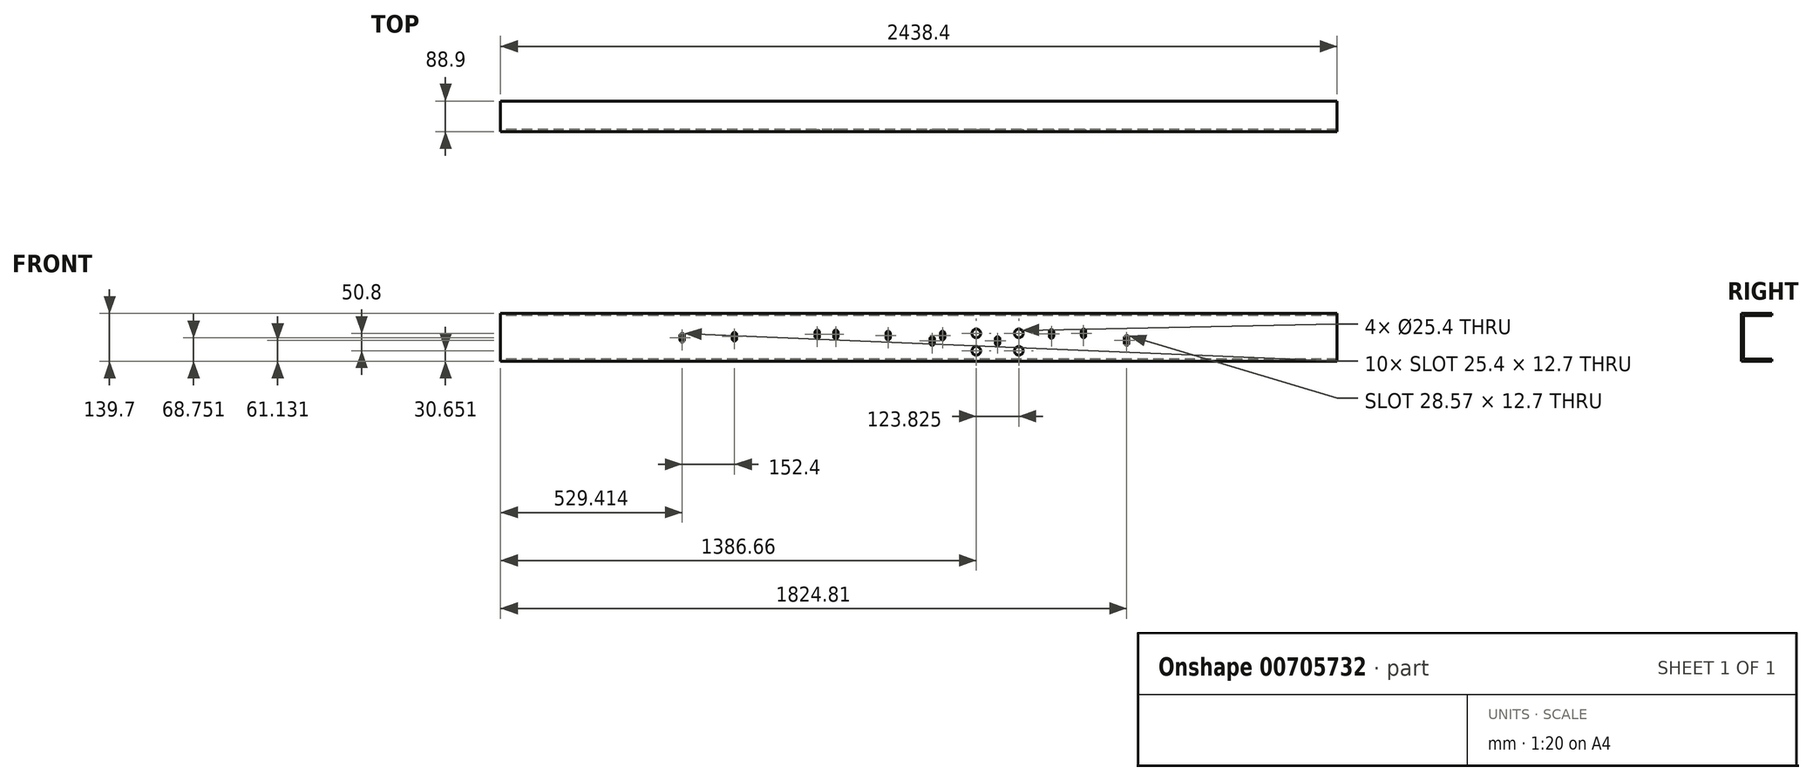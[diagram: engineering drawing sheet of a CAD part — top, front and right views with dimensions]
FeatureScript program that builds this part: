
annotation { "Feature Type Name" : "Feature", "Feature Type Description" : "" }
export const myFeature = defineFeature(function(context is Context, id is Id, definition is map)
    precondition{}
    {
        {
            var Q0;
            Q0=qCreatedBy(makeId("Right.planeOp"),FACE);
            var sketch = newSketch(context, id + "F0", { "sketchPlane" : qUnion([Q0])});
            skLineSegment(sketch, "E0.bottom", {"start": v(44.45, 69.85) * mm, "end": v(-44.45, 69.85) * mm});
            skLineSegment(sketch, "E0.top", {"start": v(44.45, -69.85) * mm, "end": v(-44.45, -69.85) * mm});
            skLineSegment(sketch, "E0.left", {"start": v(44.45, 69.85) * mm, "end": v(44.45, -69.85) * mm});
            skLineSegment(sketch, "E0.right", {"start": v(-44.45, 69.85) * mm, "end": v(-44.45, -69.85) * mm});
            skPoint(sketch, "E0.middle", {"position": v(0, 0) * mm});
            skSolve(sketch);
        }
        {
            var Q0;
            Q0 = qSketchRegion(id + "F0", true);
            extrude(context, id + "F1", {"entities" : qUnion([Q0]), "depth" : 2438.4 * mm, "offsetDistance" : 25.4 * mm, "symmetric" : true});
        }
        {
            var Q0;
            Q0=makeQuery(id+"F1.opExtrude","CAP_FACE",FACE,{"disambiguationData":[OSD([sQuery(id+"F0.wireOp",EDGE,"E0.bottom"),sQuery(id+"F0.wireOp",EDGE,"E0.top"),sQuery(id+"F0.wireOp",EDGE,"E0.left"),sQuery(id+"F0.wireOp",EDGE,"E0.right")])],"isStart":true});
            var sketch = newSketch(context, id + "F2", { "sketchPlane" : qUnion([Q0])});
            skLineSegment(sketch, "E1", {"start": v(-44.45, 63.5) * mm, "end": v(38.1, 63.5) * mm});
            skLineSegment(sketch, "E2", {"start": v(38.1, 63.5) * mm, "end": v(38.1, -63.5) * mm});
            skLineSegment(sketch, "E3", {"start": v(38.1, -63.5) * mm, "end": v(-44.45, -63.5) * mm});
            skSolve(sketch);
        }
        {
            var Q0;
            {var subQ0=sQuery(id+"F2.wireOp",EDGE,"E1");Q0=makeQuery(id+"F2.imprint","IMPRINT",FACE,{"disambiguationData":[TD([[makeQuery(id+"F2.imprint","IMPRINT",EDGE,{"derivedFrom":subQ0}),-1.0]])]});}
            extrude(context, id + "F3", {"entities" : qUnion([Q0]), "operationType" : NewBodyOperationType.REMOVE, "endBound" : BoundingType.THROUGH_ALL, "oppositeDirection" : true, "depth" : 25.4 * mm, "offsetDistance" : 25.4 * mm});
        }
        {
            var Q0;
            Q0=makeQuery(id+"F1.opExtrude","SWEPT_FACE",FACE,{"disambiguationData":[OSD([sQuery(id+"F0.wireOp",EDGE,"E0.right")])]});
            var sketch = newSketch(context, id + "F4", { "sketchPlane" : qUnion([Q0])});
            skLineSegment(sketch, "E4.bottom", {"start": v(-689.79, 11.6) * mm, "end": v(-689.79, 11.6) * mm});
            skLineSegment(sketch, "E4.top", {"start": v(-689.79, -13.8) * mm, "end": v(-689.79, -13.8) * mm});
            skLineSegment(sketch, "E4.left", {"start": v(-696.14, 5.25) * mm, "end": v(-696.14, -7.45) * mm});
            skLineSegment(sketch, "E4.right", {"start": v(-683.44, 5.25) * mm, "end": v(-683.44, -7.45) * mm});
            skPoint(sketch, "E4.middle", {"position": v(-689.79, -1.1) * mm});
            skPoint(sketch, "E4.middle.positionSnap0", {"position": v(-689.79, -14.24) * mm});
            skPoint(sketch, "E4.middle.positionSnap1", {"position": v(-696.33, -1.1) * mm});
            skPoint(sketch, "E4.centerSnap0", {"position": v(-689.79, -14.24) * mm});
            skPoint(sketch, "E4.centerSnap1", {"position": v(-696.33, -1.1) * mm});
            skLineSegment(sketch, "E5.bottom", {"start": v(-537.39, 14.78) * mm, "end": v(-537.39, 14.78) * mm});
            skLineSegment(sketch, "E5.top", {"start": v(-537.39, -10.62) * mm, "end": v(-537.39, -10.62) * mm});
            skLineSegment(sketch, "E5.left", {"start": v(-543.74, 8.43) * mm, "end": v(-543.74, -4.27) * mm});
            skLineSegment(sketch, "E5.right", {"start": v(-531.04, 8.43) * mm, "end": v(-531.04, -4.27) * mm});
            skPoint(sketch, "E5.middle", {"position": v(-537.39, 2.08) * mm});
            skPoint(sketch, "E5.middle.positionSnap0", {"position": v(-537.39, -11.13) * mm});
            skPoint(sketch, "E5.middle.positionSnap1", {"position": v(-543.99, 2.08) * mm});
            skPoint(sketch, "E5.centerSnap0", {"position": v(-537.39, -11.13) * mm});
            skPoint(sketch, "E5.centerSnap1", {"position": v(-543.99, 2.08) * mm});
            skLineSegment(sketch, "E6.bottom", {"start": v(-296.09, 21.38) * mm, "end": v(-296.09, 21.38) * mm});
            skLineSegment(sketch, "E6.top", {"start": v(-296.09, -4.02) * mm, "end": v(-296.09, -4.02) * mm});
            skLineSegment(sketch, "E6.left", {"start": v(-302.44, 15.03) * mm, "end": v(-302.44, 2.33) * mm});
            skLineSegment(sketch, "E6.right", {"start": v(-289.74, 15.03) * mm, "end": v(-289.74, 2.33) * mm});
            skPoint(sketch, "E6.middle", {"position": v(-296.09, 8.68) * mm});
            skPoint(sketch, "E6.middle.positionSnap0", {"position": v(-296.09, -4.53) * mm});
            skPoint(sketch, "E6.middle.positionSnap1", {"position": v(-302.69, 8.68) * mm});
            skPoint(sketch, "E6.centerSnap0", {"position": v(-296.09, -4.53) * mm});
            skPoint(sketch, "E6.centerSnap1", {"position": v(-302.69, 8.68) * mm});
            skLineSegment(sketch, "E7.bottom", {"start": v(-242.11, 21.38) * mm, "end": v(-242.11, 21.38) * mm});
            skLineSegment(sketch, "E7.top", {"start": v(-242.11, -4.02) * mm, "end": v(-242.11, -4.02) * mm});
            skLineSegment(sketch, "E7.left", {"start": v(-248.46, 15.03) * mm, "end": v(-248.46, 2.33) * mm});
            skLineSegment(sketch, "E7.right", {"start": v(-235.76, 15.03) * mm, "end": v(-235.76, 2.33) * mm});
            skPoint(sketch, "E7.middle", {"position": v(-242.11, 8.68) * mm});
            skPoint(sketch, "E7.middle.positionSnap0", {"position": v(-242.11, -4.53) * mm});
            skPoint(sketch, "E7.middle.positionSnap1", {"position": v(-248.71, 8.68) * mm});
            skPoint(sketch, "E7.centerSnap0", {"position": v(-242.11, -4.53) * mm});
            skPoint(sketch, "E7.centerSnap1", {"position": v(-248.71, 8.68) * mm});
            skLineSegment(sketch, "E8.bottom", {"start": v(-89.71, 17.95) * mm, "end": v(-89.71, 17.95) * mm});
            skLineSegment(sketch, "E8.top", {"start": v(-89.71, -7.45) * mm, "end": v(-89.71, -7.45) * mm});
            skLineSegment(sketch, "E8.left", {"start": v(-96.06, 11.6) * mm, "end": v(-96.06, -1.1) * mm});
            skLineSegment(sketch, "E8.right", {"start": v(-83.36, 11.6) * mm, "end": v(-83.36, -1.1) * mm});
            skPoint(sketch, "E8.middle", {"position": v(-89.71, 5.25) * mm});
            skPoint(sketch, "E8.middle.positionSnap0", {"position": v(-89.71, -7.96) * mm});
            skPoint(sketch, "E8.middle.positionSnap1", {"position": v(-96.31, 5.25) * mm});
            skPoint(sketch, "E8.centerSnap0", {"position": v(-89.71, -7.96) * mm});
            skPoint(sketch, "E8.centerSnap1", {"position": v(-96.31, 5.25) * mm});
            skLineSegment(sketch, "E9.bottom", {"start": v(38.88, 2.08) * mm, "end": v(38.88, 2.08) * mm});
            skLineSegment(sketch, "E9.top", {"start": v(38.88, -23.32) * mm, "end": v(38.88, -23.32) * mm});
            skLineSegment(sketch, "E9.left", {"start": v(32.53, -4.27) * mm, "end": v(32.53, -16.97) * mm});
            skLineSegment(sketch, "E9.right", {"start": v(45.23, -4.27) * mm, "end": v(45.23, -16.97) * mm});
            skPoint(sketch, "E9.middle", {"position": v(38.88, -10.62) * mm});
            skPoint(sketch, "E9.middle.positionSnap0", {"position": v(38.88, -23.83) * mm});
            skPoint(sketch, "E9.middle.positionSnap1", {"position": v(32.27, -10.62) * mm});
            skPoint(sketch, "E9.centerSnap0", {"position": v(38.88, -23.83) * mm});
            skPoint(sketch, "E9.centerSnap1", {"position": v(32.27, -10.62) * mm});
            skLineSegment(sketch, "E10.bottom", {"start": v(69.04, 17.95) * mm, "end": v(69.04, 17.95) * mm});
            skLineSegment(sketch, "E10.top", {"start": v(69.04, -7.45) * mm, "end": v(69.04, -7.45) * mm});
            skLineSegment(sketch, "E10.left", {"start": v(62.69, 11.6) * mm, "end": v(62.69, -1.1) * mm});
            skLineSegment(sketch, "E10.right", {"start": v(75.39, 11.6) * mm, "end": v(75.39, -1.1) * mm});
            skPoint(sketch, "E10.middle", {"position": v(69.04, 5.25) * mm});
            skPoint(sketch, "E10.middle.positionSnap0", {"position": v(69.04, -7.96) * mm});
            skPoint(sketch, "E10.middle.positionSnap1", {"position": v(62.44, 5.25) * mm});
            skPoint(sketch, "E10.centerSnap0", {"position": v(69.04, -7.96) * mm});
            skPoint(sketch, "E10.centerSnap1", {"position": v(62.44, 5.25) * mm});
            skLineSegment(sketch, "E11.bottom", {"start": v(229.38, 2.08) * mm, "end": v(229.38, 2.08) * mm});
            skLineSegment(sketch, "E11.top", {"start": v(229.38, -23.32) * mm, "end": v(229.38, -23.32) * mm});
            skLineSegment(sketch, "E11.left", {"start": v(223.03, -4.27) * mm, "end": v(223.03, -16.97) * mm});
            skLineSegment(sketch, "E11.right", {"start": v(235.73, -4.27) * mm, "end": v(235.73, -16.97) * mm});
            skPoint(sketch, "E11.middle", {"position": v(229.38, -10.62) * mm});
            skPoint(sketch, "E11.middle.positionSnap0", {"position": v(229.38, -23.83) * mm});
            skPoint(sketch, "E11.middle.positionSnap1", {"position": v(222.77, -10.62) * mm});
            skPoint(sketch, "E11.centerSnap0", {"position": v(229.38, -23.83) * mm});
            skPoint(sketch, "E11.centerSnap1", {"position": v(222.77, -10.62) * mm});
            skLineSegment(sketch, "E12.bottom", {"start": v(386.54, 22.71) * mm, "end": v(386.54, 22.71) * mm});
            skLineSegment(sketch, "E12.top", {"start": v(386.54, -2.69) * mm, "end": v(386.54, -2.69) * mm});
            skLineSegment(sketch, "E12.left", {"start": v(380.19, 16.36) * mm, "end": v(380.19, 3.66) * mm});
            skLineSegment(sketch, "E12.right", {"start": v(392.89, 16.36) * mm, "end": v(392.89, 3.66) * mm});
            skPoint(sketch, "E12.middle", {"position": v(386.54, 10.01) * mm});
            skPoint(sketch, "E12.middle.positionSnap0", {"position": v(386.54, -3.2) * mm});
            skPoint(sketch, "E12.middle.positionSnap1", {"position": v(379.94, 10.01) * mm});
            skPoint(sketch, "E12.centerSnap0", {"position": v(386.54, -3.2) * mm});
            skPoint(sketch, "E12.centerSnap1", {"position": v(379.94, 10.01) * mm});
            skLineSegment(sketch, "E13.bottom", {"start": v(480.2, 24.3) * mm, "end": v(480.2, 24.3) * mm});
            skLineSegment(sketch, "E13.top", {"start": v(480.2, -1.1) * mm, "end": v(480.2, -1.1) * mm});
            skLineSegment(sketch, "E13.left", {"start": v(473.85, 17.95) * mm, "end": v(473.85, 5.25) * mm});
            skLineSegment(sketch, "E13.right", {"start": v(486.55, 17.95) * mm, "end": v(486.55, 5.25) * mm});
            skPoint(sketch, "E13.middle", {"position": v(480.2, 11.6) * mm});
            skPoint(sketch, "E13.middle.positionSnap0", {"position": v(480.2, -1.6) * mm});
            skPoint(sketch, "E13.middle.positionSnap1", {"position": v(473.6, 11.6) * mm});
            skPoint(sketch, "E13.centerSnap0", {"position": v(480.2, -1.6) * mm});
            skPoint(sketch, "E13.centerSnap1", {"position": v(473.6, 11.6) * mm});
            skLineSegment(sketch, "E14.bottom", {"start": v(605.61, 5.57) * mm, "end": v(605.61, 5.57) * mm});
            skLineSegment(sketch, "E14.top", {"start": v(605.61, -23) * mm, "end": v(605.61, -23) * mm});
            skLineSegment(sketch, "E14.left", {"start": v(599.26, -0.78) * mm, "end": v(599.26, -16.66) * mm});
            skLineSegment(sketch, "E14.right", {"start": v(611.96, -0.78) * mm, "end": v(611.96, -16.66) * mm});
            skPoint(sketch, "E14.middle", {"position": v(605.61, -8.72) * mm});
            skPoint(sketch, "E14.middle.positionSnap0", {"position": v(605.61, -23.26) * mm});
            skPoint(sketch, "E14.middle.positionSnap1", {"position": v(599.01, -8.72) * mm});
            skPoint(sketch, "E14.centerSnap0", {"position": v(605.61, -23.26) * mm});
            skPoint(sketch, "E14.centerSnap1", {"position": v(599.01, -8.72) * mm});
            skCircle(sketch, "E15", {"center": v(167.46, 11.6) * mm, "radius": 12.7 * mm});
            skCircle(sketch, "E16", {"center": v(291.29, 11.6) * mm, "radius": 12.7 * mm});
            skCircle(sketch, "E17", {"center": v(291.29, -39.2) * mm, "radius": 12.7 * mm});
            skCircle(sketch, "E18", {"center": v(167.46, -39.2) * mm, "radius": 12.7 * mm});
            skPoint(sketch, "E19.visualSharp", {"position": v(-696.14, 11.6) * mm});
            skArc(sketch, "E19.filletArc", {"start": v(-689.79, 11.6) * mm, "mid": v(-694.28, 9.74) * mm, "end": v(-696.14, 5.25) * mm});
            skPoint(sketch, "E20.visualSharp", {"position": v(-683.44, 11.6) * mm});
            skArc(sketch, "E20.filletArc", {"start": v(-683.44, 5.25) * mm, "mid": v(-685.3, 9.74) * mm, "end": v(-689.79, 11.6) * mm});
            skPoint(sketch, "E21.visualSharp", {"position": v(-696.14, -13.8) * mm});
            skArc(sketch, "E21.filletArc", {"start": v(-696.14, -7.45) * mm, "mid": v(-694.28, -11.94) * mm, "end": v(-689.79, -13.8) * mm});
            skPoint(sketch, "E22.visualSharp", {"position": v(-683.44, -13.8) * mm});
            skArc(sketch, "E22.filletArc", {"start": v(-689.79, -13.8) * mm, "mid": v(-685.3, -11.94) * mm, "end": v(-683.44, -7.45) * mm});
            skPoint(sketch, "E23.visualSharp", {"position": v(-543.74, 14.78) * mm});
            skArc(sketch, "E23.filletArc", {"start": v(-537.39, 14.78) * mm, "mid": v(-541.88, 12.92) * mm, "end": v(-543.74, 8.43) * mm});
            skPoint(sketch, "E24.visualSharp", {"position": v(-531.04, 14.78) * mm});
            skArc(sketch, "E24.filletArc", {"start": v(-531.04, 8.43) * mm, "mid": v(-532.9, 12.92) * mm, "end": v(-537.39, 14.78) * mm});
            skPoint(sketch, "E25.visualSharp", {"position": v(-543.74, -10.62) * mm});
            skArc(sketch, "E25.filletArc", {"start": v(-543.74, -4.27) * mm, "mid": v(-541.88, -8.76) * mm, "end": v(-537.39, -10.62) * mm});
            skPoint(sketch, "E26.visualSharp", {"position": v(-531.04, -10.62) * mm});
            skArc(sketch, "E26.filletArc", {"start": v(-537.39, -10.62) * mm, "mid": v(-532.9, -8.76) * mm, "end": v(-531.04, -4.27) * mm});
            skPoint(sketch, "E27.visualSharp", {"position": v(-302.44, 21.38) * mm});
            skArc(sketch, "E27.filletArc", {"start": v(-296.09, 21.38) * mm, "mid": v(-300.58, 19.52) * mm, "end": v(-302.44, 15.03) * mm});
            skPoint(sketch, "E28.visualSharp", {"position": v(-248.46, 21.38) * mm});
            skArc(sketch, "E28.filletArc", {"start": v(-242.11, 21.38) * mm, "mid": v(-246.6, 19.52) * mm, "end": v(-248.46, 15.03) * mm});
            skPoint(sketch, "E29.visualSharp", {"position": v(-302.44, -4.02) * mm});
            skArc(sketch, "E29.filletArc", {"start": v(-302.44, 2.33) * mm, "mid": v(-300.58, -2.16) * mm, "end": v(-296.09, -4.02) * mm});
            skPoint(sketch, "E30.visualSharp", {"position": v(-248.46, -4.02) * mm});
            skArc(sketch, "E30.filletArc", {"start": v(-248.46, 2.33) * mm, "mid": v(-246.6, -2.16) * mm, "end": v(-242.11, -4.02) * mm});
            skPoint(sketch, "E31.visualSharp", {"position": v(-235.76, -4.02) * mm});
            skArc(sketch, "E31.filletArc", {"start": v(-242.11, -4.02) * mm, "mid": v(-237.62, -2.16) * mm, "end": v(-235.76, 2.33) * mm});
            skPoint(sketch, "E32.visualSharp", {"position": v(-235.76, 21.38) * mm});
            skArc(sketch, "E32.filletArc", {"start": v(-235.76, 15.03) * mm, "mid": v(-237.62, 19.52) * mm, "end": v(-242.11, 21.38) * mm});
            skPoint(sketch, "E33.visualSharp", {"position": v(-289.74, 21.38) * mm});
            skArc(sketch, "E33.filletArc", {"start": v(-289.74, 15.03) * mm, "mid": v(-291.6, 19.52) * mm, "end": v(-296.09, 21.38) * mm});
            skPoint(sketch, "E34.visualSharp", {"position": v(-289.74, -4.02) * mm});
            skArc(sketch, "E34.filletArc", {"start": v(-296.09, -4.02) * mm, "mid": v(-291.6, -2.16) * mm, "end": v(-289.74, 2.33) * mm});
            skPoint(sketch, "E35.visualSharp", {"position": v(-96.06, 17.95) * mm});
            skArc(sketch, "E35.filletArc", {"start": v(-89.71, 17.95) * mm, "mid": v(-94.2, 16.1) * mm, "end": v(-96.06, 11.6) * mm});
            skPoint(sketch, "E36.visualSharp", {"position": v(-83.36, 17.95) * mm});
            skArc(sketch, "E36.filletArc", {"start": v(-83.36, 11.6) * mm, "mid": v(-85.22, 16.1) * mm, "end": v(-89.71, 17.95) * mm});
            skPoint(sketch, "E37.visualSharp", {"position": v(-96.06, -7.45) * mm});
            skArc(sketch, "E37.filletArc", {"start": v(-96.06, -1.1) * mm, "mid": v(-94.2, -5.59) * mm, "end": v(-89.71, -7.45) * mm});
            skPoint(sketch, "E38.visualSharp", {"position": v(-83.36, -7.45) * mm});
            skArc(sketch, "E38.filletArc", {"start": v(-89.71, -7.45) * mm, "mid": v(-85.22, -5.59) * mm, "end": v(-83.36, -1.1) * mm});
            skPoint(sketch, "E39.visualSharp", {"position": v(32.53, 2.08) * mm});
            skArc(sketch, "E39.filletArc", {"start": v(38.88, 2.08) * mm, "mid": v(34.39, 0.22) * mm, "end": v(32.53, -4.27) * mm});
            skPoint(sketch, "E40.visualSharp", {"position": v(45.23, 2.08) * mm});
            skArc(sketch, "E40.filletArc", {"start": v(45.23, -4.27) * mm, "mid": v(43.37, 0.22) * mm, "end": v(38.88, 2.08) * mm});
            skPoint(sketch, "E41.visualSharp", {"position": v(45.23, -23.32) * mm});
            skArc(sketch, "E41.filletArc", {"start": v(38.88, -23.32) * mm, "mid": v(43.37, -21.46) * mm, "end": v(45.23, -16.97) * mm});
            skPoint(sketch, "E42.visualSharp", {"position": v(32.53, -23.32) * mm});
            skArc(sketch, "E42.filletArc", {"start": v(32.53, -16.97) * mm, "mid": v(34.39, -21.46) * mm, "end": v(38.88, -23.32) * mm});
            skPoint(sketch, "E43.visualSharp", {"position": v(62.69, 17.95) * mm});
            skArc(sketch, "E43.filletArc", {"start": v(69.04, 17.95) * mm, "mid": v(64.55, 16.1) * mm, "end": v(62.69, 11.6) * mm});
            skPoint(sketch, "E44.visualSharp", {"position": v(75.39, -7.45) * mm});
            skArc(sketch, "E44.filletArc", {"start": v(69.04, -7.45) * mm, "mid": v(73.53, -5.59) * mm, "end": v(75.39, -1.1) * mm});
            skPoint(sketch, "E45.visualSharp", {"position": v(62.69, -7.45) * mm});
            skArc(sketch, "E45.filletArc", {"start": v(62.69, -1.1) * mm, "mid": v(64.55, -5.59) * mm, "end": v(69.04, -7.45) * mm});
            skPoint(sketch, "E46.visualSharp", {"position": v(75.39, 17.95) * mm});
            skArc(sketch, "E46.filletArc", {"start": v(75.39, 11.6) * mm, "mid": v(73.53, 16.1) * mm, "end": v(69.04, 17.95) * mm});
            skPoint(sketch, "E47.visualSharp", {"position": v(223.03, 2.08) * mm});
            skArc(sketch, "E47.filletArc", {"start": v(229.38, 2.08) * mm, "mid": v(224.89, 0.22) * mm, "end": v(223.03, -4.27) * mm});
            skPoint(sketch, "E48.visualSharp", {"position": v(235.73, 2.08) * mm});
            skArc(sketch, "E48.filletArc", {"start": v(235.73, -4.27) * mm, "mid": v(233.87, 0.22) * mm, "end": v(229.38, 2.08) * mm});
            skPoint(sketch, "E49.visualSharp", {"position": v(235.73, -23.32) * mm});
            skArc(sketch, "E49.filletArc", {"start": v(229.38, -23.32) * mm, "mid": v(233.87, -21.46) * mm, "end": v(235.73, -16.97) * mm});
            skPoint(sketch, "E50.visualSharp", {"position": v(223.03, -23.32) * mm});
            skArc(sketch, "E50.filletArc", {"start": v(223.03, -16.97) * mm, "mid": v(224.89, -21.46) * mm, "end": v(229.38, -23.32) * mm});
            skPoint(sketch, "E51.visualSharp", {"position": v(380.19, 22.71) * mm});
            skArc(sketch, "E51.filletArc", {"start": v(386.54, 22.71) * mm, "mid": v(382.05, 20.85) * mm, "end": v(380.19, 16.36) * mm});
            skPoint(sketch, "E52.visualSharp", {"position": v(380.19, -2.69) * mm});
            skArc(sketch, "E52.filletArc", {"start": v(380.19, 3.66) * mm, "mid": v(382.05, -0.83) * mm, "end": v(386.54, -2.69) * mm});
            skPoint(sketch, "E53.visualSharp", {"position": v(392.89, -2.69) * mm});
            skArc(sketch, "E53.filletArc", {"start": v(386.54, -2.69) * mm, "mid": v(391.03, -0.83) * mm, "end": v(392.89, 3.66) * mm});
            skPoint(sketch, "E54.visualSharp", {"position": v(392.89, 22.71) * mm});
            skArc(sketch, "E54.filletArc", {"start": v(392.89, 16.36) * mm, "mid": v(391.03, 20.85) * mm, "end": v(386.54, 22.71) * mm});
            skPoint(sketch, "E55.visualSharp", {"position": v(473.85, 24.3) * mm});
            skArc(sketch, "E55.filletArc", {"start": v(480.2, 24.3) * mm, "mid": v(475.71, 22.44) * mm, "end": v(473.85, 17.95) * mm});
            skPoint(sketch, "E56.visualSharp", {"position": v(486.55, 24.3) * mm});
            skArc(sketch, "E56.filletArc", {"start": v(486.55, 17.95) * mm, "mid": v(484.7, 22.44) * mm, "end": v(480.2, 24.3) * mm});
            skPoint(sketch, "E57.visualSharp", {"position": v(486.55, -1.1) * mm});
            skArc(sketch, "E57.filletArc", {"start": v(480.2, -1.1) * mm, "mid": v(484.7, 0.76) * mm, "end": v(486.55, 5.25) * mm});
            skPoint(sketch, "E58.visualSharp", {"position": v(473.85, -1.1) * mm});
            skArc(sketch, "E58.filletArc", {"start": v(473.85, 5.25) * mm, "mid": v(475.71, 0.76) * mm, "end": v(480.2, -1.1) * mm});
            skPoint(sketch, "E59.visualSharp", {"position": v(599.26, 5.57) * mm});
            skArc(sketch, "E59.filletArc", {"start": v(605.61, 5.57) * mm, "mid": v(601.12, 3.7) * mm, "end": v(599.26, -0.78) * mm});
            skPoint(sketch, "E60.visualSharp", {"position": v(611.96, -23) * mm});
            skArc(sketch, "E60.filletArc", {"start": v(605.61, -23) * mm, "mid": v(610.1, -21.15) * mm, "end": v(611.96, -16.66) * mm});
            skPoint(sketch, "E61.visualSharp", {"position": v(599.26, -23) * mm});
            skArc(sketch, "E61.filletArc", {"start": v(599.26, -16.66) * mm, "mid": v(601.12, -21.15) * mm, "end": v(605.61, -23) * mm});
            skPoint(sketch, "E62.visualSharp", {"position": v(611.96, 5.57) * mm});
            skArc(sketch, "E62.filletArc", {"start": v(611.96, -0.78) * mm, "mid": v(610.1, 3.7) * mm, "end": v(605.61, 5.57) * mm});
            skSolve(sketch);
        }
        {
            var Q0;
            Q0 = qSketchRegion(id + "F4", true);
            extrude(context, id + "F5", {"entities" : qUnion([Q0]), "operationType" : NewBodyOperationType.REMOVE, "endBound" : BoundingType.THROUGH_ALL, "oppositeDirection" : true, "depth" : 25.4 * mm, "offsetDistance" : 25.4 * mm});
        }
    });
